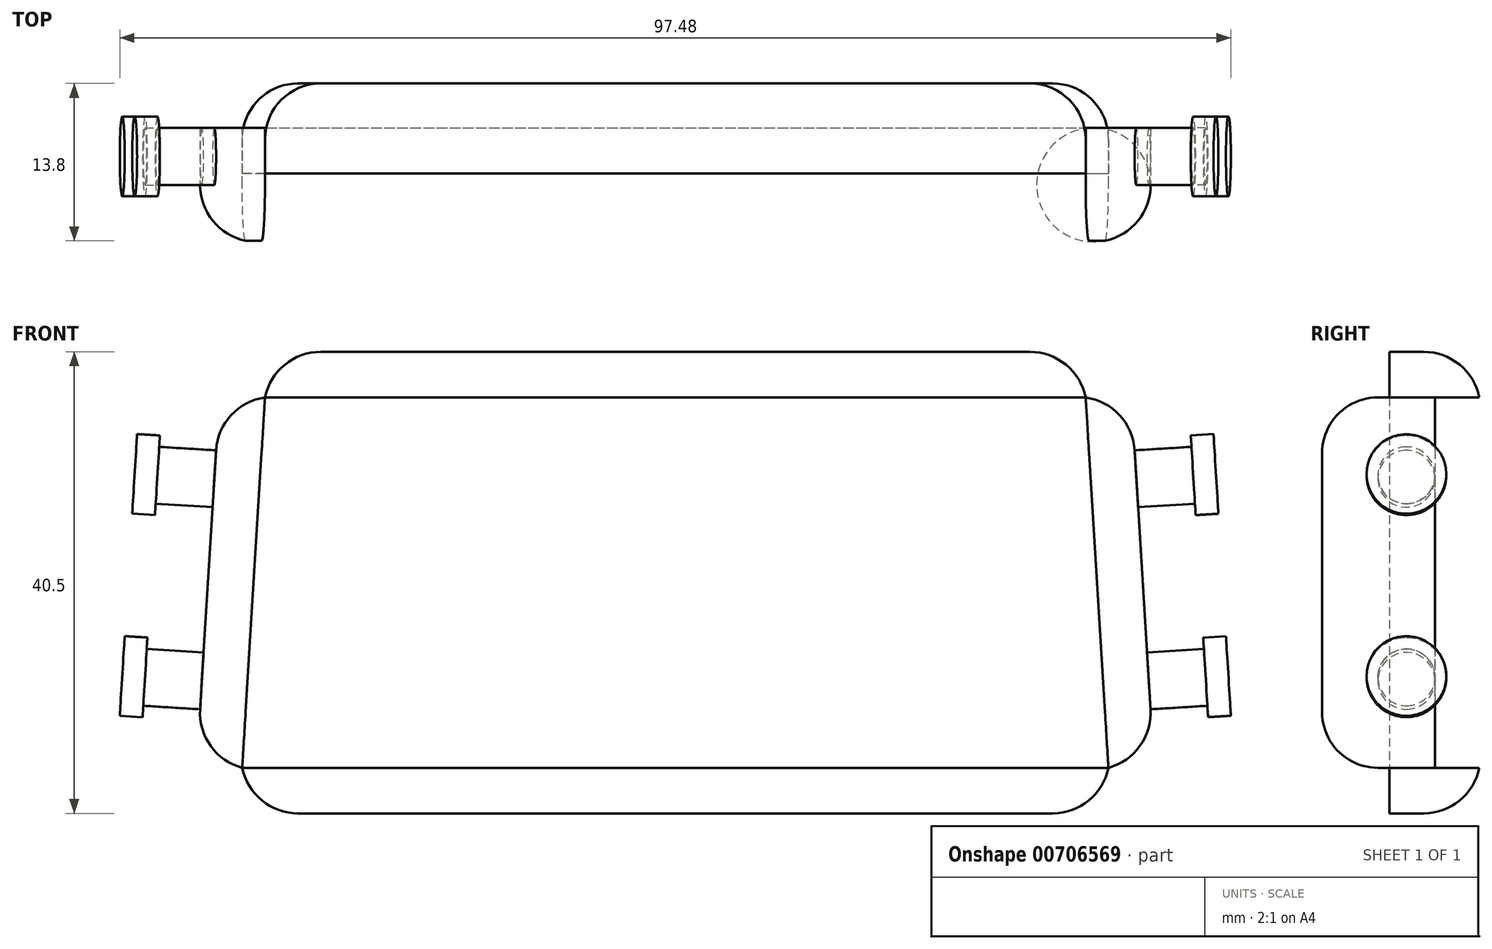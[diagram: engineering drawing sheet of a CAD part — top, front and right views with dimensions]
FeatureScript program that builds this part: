
annotation { "Feature Type Name" : "Feature", "Feature Type Description" : "" }
export const myFeature = defineFeature(function(context is Context, id is Id, definition is map)
    precondition{}
    {
        {
            var Q0;
            Q0=qCreatedBy(makeId("Front.planeOp"),FACE);
            var sketch = newSketch(context, id + "F0", { "sketchPlane" : qUnion([Q0])});
            skLineSegment(sketch, "E0", {"start": v(-36, 32.5) * mm, "end": v(36, 32.5) * mm});
            skLineSegment(sketch, "E1", {"start": v(-38, 0) * mm, "end": v(38, 0) * mm});
            skLineSegment(sketch, "E2", {"start": v(-36, 32.5) * mm, "end": v(-38, 0) * mm});
            skLineSegment(sketch, "E3", {"start": v(36, 32.5) * mm, "end": v(38, 0) * mm});
            skLineSegment(sketch, "E4", {"start": v(-36, 32.5) * mm, "end": v(-40, 32.75) * mm});
            skLineSegment(sketch, "E5", {"start": v(-38, 0) * mm, "end": v(-42, 0.25) * mm});
            skLineSegment(sketch, "E6", {"start": v(-42, 0.25) * mm, "end": v(-40, 32.75) * mm});
            skLineSegment(sketch, "E7", {"start": v(36, 32.5) * mm, "end": v(40, 32.75) * mm});
            skLineSegment(sketch, "E8", {"start": v(40, 32.75) * mm, "end": v(42, 0.25) * mm});
            skLineSegment(sketch, "E9", {"start": v(42, 0.25) * mm, "end": v(38, 0) * mm});
            skLineSegment(sketch, "E10", {"start": v(-38, 0) * mm, "end": v(-38, -4) * mm});
            skLineSegment(sketch, "E11", {"start": v(-38, -4) * mm, "end": v(38, -4) * mm});
            skLineSegment(sketch, "E12", {"start": v(38, -4) * mm, "end": v(38, 0) * mm});
            skLineSegment(sketch, "E13", {"start": v(-36, 32.5) * mm, "end": v(-36, 36.5) * mm});
            skLineSegment(sketch, "E14", {"start": v(-36, 36.5) * mm, "end": v(36, 36.5) * mm});
            skLineSegment(sketch, "E15", {"start": v(36, 36.5) * mm, "end": v(36, 32.5) * mm});
            skSolve(sketch);
        }
        {
            var Q0;
            Q0=makeQuery(id+"F0.imprint","IMPRINT",FACE,{"disambiguationData":[TD([[makeQuery(id+"F0.imprint","IMPRINT",EDGE,{"derivedFrom":sQuery(id+"F0.wireOp",EDGE,"E1")}),-1.0]])]});
            extrude(context, id + "F1", {"entities" : qUnion([Q0]), "oppositeDirection" : true, "depth" : 4 * mm, "offsetDistance" : 25 * mm, "hasSecondDirection" : true, "secondDirectionOppositeDirection" : false, "secondDirectionDepth" : 4 * mm});
        }
        {
            var Q0;
            Q0=makeQuery(id+"F0.imprint","IMPRINT",FACE,{"disambiguationData":[TD([[makeQuery(id+"F0.imprint","IMPRINT",EDGE,{"derivedFrom":sQuery(id+"F0.wireOp",EDGE,"E0")}),1.0]])]});
            extrude(context, id + "F2", {"entities" : qUnion([Q0]), "oppositeDirection" : true, "depth" : 4 * mm, "offsetDistance" : 25 * mm, "hasSecondDirection" : true, "secondDirectionOppositeDirection" : false, "secondDirectionDepth" : 4 * mm});
        }
        {
            var Q0;
            Q0=makeQuery(id+"F0.imprint","IMPRINT",FACE,{"disambiguationData":[TD([[makeQuery(id+"F0.imprint","IMPRINT",EDGE,{"derivedFrom":sQuery(id+"F0.wireOp",EDGE,"E2")}),-1.0]])]});
            extrude(context, id + "F3", {"entities" : qUnion([Q0]), "operationType" : NewBodyOperationType.ADD, "depth" : 10 * mm, "offsetDistance" : 25 * mm});
        }
        {
            var Q0;
            Q0=makeQuery(id+"F0.imprint","IMPRINT",FACE,{"disambiguationData":[TD([[makeQuery(id+"F0.imprint","IMPRINT",EDGE,{"derivedFrom":sQuery(id+"F0.wireOp",EDGE,"E3")}),1.0]])]});
            extrude(context, id + "F4", {"entities" : qUnion([Q0]), "depth" : 10 * mm, "offsetDistance" : 25 * mm});
        }
        {
            var Q0;
            Q0=makeQuery(id+"F0.imprint","IMPRINT",FACE,{"disambiguationData":[TD([[makeQuery(id+"F0.imprint","IMPRINT",EDGE,{"derivedFrom":sQuery(id+"F0.wireOp",EDGE,"E0")}),-1.0]])]});
            extrude(context, id + "F5", {"entities" : qUnion([Q0]), "depth" : 4 * mm, "offsetDistance" : 25 * mm});
        }
        {
            var Q0;
            Q0=makeQuery(id+"F4.opExtrude","SWEPT_EDGE",EDGE,{"disambiguationData":[OSD([sQuery(id+"F0.wireOp",EDGE,"E8"),sQuery(id+"F0.wireOp",EDGE,"E9")])]});
            fillet(context, id + "F6", {"entities" : qUnion([Q0]), "radius" : 5 * mm, "tangentPropagation" : true, "allowEdgeOverflow" : false});
        }
        {
            var Q0;
            Q0=makeQuery(id+"F1.opExtrude","SWEPT_EDGE",EDGE,{"disambiguationData":[OSD([sQuery(id+"F0.wireOp",EDGE,"E11"),sQuery(id+"F0.wireOp",EDGE,"E12")])]});
            fillet(context, id + "F7", {"entities" : qUnion([Q0]), "radius" : 5 * mm, "tangentPropagation" : true, "allowEdgeOverflow" : false});
        }
        {
            var Q0;
            Q0=makeQuery(id+"F1.opExtrude","SWEPT_EDGE",EDGE,{"disambiguationData":[OSD([sQuery(id+"F0.wireOp",EDGE,"E10"),sQuery(id+"F0.wireOp",EDGE,"E11")])]});
            fillet(context, id + "F8", {"entities" : qUnion([Q0]), "radius" : 5 * mm, "tangentPropagation" : true, "allowEdgeOverflow" : false});
        }
        {
            var Q0;
            Q0=makeQuery(id+"F3.opExtrude","SWEPT_EDGE",EDGE,{"disambiguationData":[OSD([sQuery(id+"F0.wireOp",EDGE,"E5"),sQuery(id+"F0.wireOp",EDGE,"E6")])]});
            fillet(context, id + "F9", {"entities" : qUnion([Q0]), "radius" : 5 * mm, "tangentPropagation" : true, "allowEdgeOverflow" : false});
        }
        {
            var Q0;
            Q0=makeQuery(id+"F3.opExtrude","SWEPT_EDGE",EDGE,{"disambiguationData":[OSD([sQuery(id+"F0.wireOp",EDGE,"E4"),sQuery(id+"F0.wireOp",EDGE,"E6")])]});
            fillet(context, id + "F10", {"entities" : qUnion([Q0]), "radius" : 5 * mm, "tangentPropagation" : true, "allowEdgeOverflow" : false});
        }
        {
            var Q0;
            Q0=makeQuery(id+"F2.opExtrude","SWEPT_EDGE",EDGE,{"disambiguationData":[OSD([sQuery(id+"F0.wireOp",EDGE,"E13"),sQuery(id+"F0.wireOp",EDGE,"E14")])]});
            fillet(context, id + "F11", {"entities" : qUnion([Q0]), "radius" : 5 * mm, "tangentPropagation" : true, "allowEdgeOverflow" : false});
        }
        {
            var Q0;
            Q0=makeQuery(id+"F2.opExtrude","SWEPT_EDGE",EDGE,{"disambiguationData":[OSD([sQuery(id+"F0.wireOp",EDGE,"E14"),sQuery(id+"F0.wireOp",EDGE,"E15")])]});
            fillet(context, id + "F12", {"entities" : qUnion([Q0]), "radius" : 5 * mm, "tangentPropagation" : true, "allowEdgeOverflow" : false});
        }
        {
            var Q0;
            Q0=makeQuery(id+"F4.opExtrude","SWEPT_EDGE",EDGE,{"disambiguationData":[OSD([sQuery(id+"F0.wireOp",EDGE,"E7"),sQuery(id+"F0.wireOp",EDGE,"E8")])]});
            fillet(context, id + "F13", {"entities" : qUnion([Q0]), "radius" : 5 * mm, "tangentPropagation" : true, "allowEdgeOverflow" : false});
        }
        {
            var Q0;
            Q0=makeQuery(id+"F4.opExtrude","CAP_EDGE",EDGE,{"disambiguationData":[OSD([sQuery(id+"F0.wireOp",EDGE,"E8")])],"isStart":false});
            fillet(context, id + "F14", {"entities" : qUnion([Q0]), "radius" : 5 * mm, "tangentPropagation" : true, "allowEdgeOverflow" : false});
        }
        {
            var Q0;
            Q0=makeQuery(id+"F3.opExtrude","CAP_EDGE",EDGE,{"disambiguationData":[OSD([sQuery(id+"F0.wireOp",EDGE,"E6")])],"isStart":false});
            fillet(context, id + "F15", {"entities" : qUnion([Q0]), "radius" : 5 * mm, "tangentPropagation" : true, "allowEdgeOverflow" : false});
        }
        {
            var Q0;
            Q0=makeQuery(id+"F2.opExtrude","CAP_EDGE",EDGE,{"disambiguationData":[OSD([sQuery(id+"F0.wireOp",EDGE,"E14")])],"isStart":false});
            fillet(context, id + "F16", {"entities" : qUnion([Q0]), "radius" : 5 * mm, "tangentPropagation" : true, "allowEdgeOverflow" : false});
        }
        {
            var Q0;
            Q0=makeQuery(id+"F1.opExtrude","CAP_EDGE",EDGE,{"disambiguationData":[OSD([sQuery(id+"F0.wireOp",EDGE,"E11")])],"isStart":false});
            fillet(context, id + "F17", {"entities" : qUnion([Q0]), "radius" : 5 * mm, "tangentPropagation" : true, "allowEdgeOverflow" : false});
        }
        {
            var Q0;
            Q0=makeQuery(id+"F3.opExtrude","SWEPT_FACE",FACE,{"disambiguationData":[OSD([sQuery(id+"F0.wireOp",EDGE,"E6")])]});
            var sketch = newSketch(context, id + "F18", { "sketchPlane" : qUnion([Q0])});
            skCircle(sketch, "E16", {"center": v(2.5, 5.06) * mm, "radius": 2.5 * mm});
            skPoint(sketch, "E16.first.point", {"position": v(5, 5.06) * mm});
            skPoint(sketch, "E16.second.point", {"position": v(2.5, 2.56) * mm});
            skPoint(sketch, "E16.third.point", {"position": v(0, 5.06) * mm});
            skCircle(sketch, "E17", {"center": v(2.5, 22.83) * mm, "radius": 2.5 * mm});
            skPoint(sketch, "E17.first.point", {"position": v(2.5, 25.33) * mm});
            skPoint(sketch, "E17.second.point", {"position": v(5, 22.83) * mm});
            skPoint(sketch, "E17.third.point", {"position": v(0, 22.83) * mm});
            skSolve(sketch);
        }
        {
            var Q0;
            {var subQ0=sQuery(id+"F18.wireOp",EDGE,"E17");var subQ1=sQuery(id+"F0.wireOp",EDGE,"E6");var subQ5=makeQuery(id+"F18.imprint","INTERSECT",VERTEX,{"derivedFrom":[makeQuery(id+"F3.opExtrude","CAP_EDGE",EDGE,{"disambiguationData":[OSD([subQ1])],"isStart":true}),subQ0]});Q0=makeQuery(id+"F18.imprint","IMPRINT",FACE,{"disambiguationData":[TD([[makeQuery(id+"F18.imprint","IMPRINT",EDGE,{"disambiguationData":[TD([[subQ5,-1.0]])],"derivedFrom":subQ0}),1.0]])]});}
            var Q1;
            {var subQ0=sQuery(id+"F18.wireOp",EDGE,"E16");var subQ1=sQuery(id+"F0.wireOp",EDGE,"E6");var subQ2=makeQuery(id+"F18.imprint","INTERSECT",VERTEX,{"derivedFrom":[makeQuery(id+"F3.opExtrude","CAP_EDGE",EDGE,{"disambiguationData":[OSD([subQ1])],"isStart":true}),subQ0]});Q1=makeQuery(id+"F18.imprint","IMPRINT",FACE,{"disambiguationData":[TD([[makeQuery(id+"F18.imprint","IMPRINT",EDGE,{"disambiguationData":[TD([[subQ2,1.0]])],"derivedFrom":subQ0}),1.0]])]});}
            var Q2;
            Q2=sQuery(id+"F18.wireOp",EDGE,"E16");
            var Q3;
            Q3=sQuery(id+"F18.wireOp",EDGE,"E17");
            extrude(context, id + "F19", {"entities" : qUnion([Q0, Q1]), "operationType" : NewBodyOperationType.ADD, "surfaceEntities" : qUnion([Q2, Q3]), "depth" : 5 * mm, "offsetDistance" : 25 * mm});
        }
        {
            var Q0;
            Q0=makeQuery(id+"F19.opExtrude","CAP_FACE",FACE,{"disambiguationData":[OSD([sQuery(id+"F18.wireOp",EDGE,"E16")])],"isStart":false});
            var sketch = newSketch(context, id + "F20", { "sketchPlane" : qUnion([Q0])});
            skCircle(sketch, "E18", {"center": v(2.5, 5.06) * mm, "radius": 3.5 * mm});
            skSolve(sketch);
        }
        {
            var Q0;
            Q0=makeQuery(id+"F20.imprint","IMPRINT",FACE,{"disambiguationData":[TD([[makeQuery(id+"F20.imprint","IMPRINT",EDGE,{"derivedFrom":sQuery(id+"F20.wireOp",EDGE,"E18")}),1.0]])]});
            var Q1;
            Q1=makeQuery(id+"F20.imprint","IMPRINT",FACE,{"disambiguationData":[TD([[makeQuery(id+"F20.imprint","IMPRINT",EDGE,{"derivedFrom":makeQuery(id+"F19.opExtrude","CAP_EDGE",EDGE,{"disambiguationData":[OSD([sQuery(id+"F18.wireOp",EDGE,"E16")])],"isStart":false})}),1.0]])]});
            var Q2;
            Q2=sQuery(id+"F20.wireOp",EDGE,"E18");
            extrude(context, id + "F21", {"entities" : qUnion([Q0, Q1]), "operationType" : NewBodyOperationType.ADD, "surfaceEntities" : qUnion([Q2]), "depth" : 2 * mm, "offsetDistance" : 25 * mm});
        }
        {
            var Q0;
            Q0=makeQuery(id+"F19.opExtrude","CAP_FACE",FACE,{"disambiguationData":[OSD([sQuery(id+"F18.wireOp",EDGE,"E17")])],"isStart":false});
            var sketch = newSketch(context, id + "F22", { "sketchPlane" : qUnion([Q0])});
            skCircle(sketch, "E19", {"center": v(2.5, 22.83) * mm, "radius": 3.5 * mm});
            skSolve(sketch);
        }
        {
            var Q0;
            Q0=makeQuery(id+"F22.imprint","IMPRINT",FACE,{"disambiguationData":[TD([[makeQuery(id+"F22.imprint","IMPRINT",EDGE,{"derivedFrom":sQuery(id+"F22.wireOp",EDGE,"E19")}),1.0]])]});
            var Q1;
            Q1=makeQuery(id+"F22.imprint","IMPRINT",FACE,{"disambiguationData":[TD([[makeQuery(id+"F22.imprint","IMPRINT",EDGE,{"derivedFrom":makeQuery(id+"F19.opExtrude","CAP_EDGE",EDGE,{"disambiguationData":[OSD([sQuery(id+"F18.wireOp",EDGE,"E17")])],"isStart":false})}),1.0]])]});
            var Q2;
            Q2=sQuery(id+"F22.wireOp",EDGE,"E19");
            extrude(context, id + "F23", {"entities" : qUnion([Q0, Q1]), "operationType" : NewBodyOperationType.ADD, "surfaceEntities" : qUnion([Q2]), "depth" : 2 * mm, "offsetDistance" : 25 * mm});
        }
        {
            var Q0;
            Q0=makeQuery(id+"F4.opExtrude","SWEPT_FACE",FACE,{"disambiguationData":[OSD([sQuery(id+"F0.wireOp",EDGE,"E8")])]});
            var sketch = newSketch(context, id + "F24", { "sketchPlane" : qUnion([Q0])});
            skCircle(sketch, "E20", {"center": v(-2.5, 5.06) * mm, "radius": 2.5 * mm});
            skPoint(sketch, "E20.first.point", {"position": v(-2.5, 2.56) * mm});
            skPoint(sketch, "E20.second.point", {"position": v(-5, 5.06) * mm});
            skPoint(sketch, "E20.third.point", {"position": v(0, 5.06) * mm});
            skCircle(sketch, "E21", {"center": v(-2.5, 22.83) * mm, "radius": 2.5 * mm});
            skPoint(sketch, "E21.first.point", {"position": v(-2.5, 25.33) * mm});
            skPoint(sketch, "E21.second.point", {"position": v(0, 22.83) * mm});
            skPoint(sketch, "E21.third.point", {"position": v(-5, 22.83) * mm});
            skSolve(sketch);
        }
        {
            var Q0;
            {var subQ0=sQuery(id+"F24.wireOp",EDGE,"E20");var subQ1=sQuery(id+"F0.wireOp",EDGE,"E8");var subQ4=makeQuery(id+"F24.imprint","INTERSECT",VERTEX,{"derivedFrom":[makeQuery(id+"F4.opExtrude","CAP_EDGE",EDGE,{"disambiguationData":[OSD([subQ1])],"isStart":true}),subQ0]});Q0=makeQuery(id+"F24.imprint","IMPRINT",FACE,{"disambiguationData":[TD([[makeQuery(id+"F24.imprint","IMPRINT",EDGE,{"disambiguationData":[TD([[subQ4,-1.0]])],"derivedFrom":subQ0}),1.0]])]});}
            var Q1;
            Q1=sQuery(id+"F24.wireOp",EDGE,"E20");
            extrude(context, id + "F25", {"entities" : qUnion([Q0]), "operationType" : NewBodyOperationType.ADD, "surfaceEntities" : qUnion([Q1]), "depth" : 5 * mm, "offsetDistance" : 25 * mm});
        }
        {
            var Q0;
            {var subQ0=sQuery(id+"F24.wireOp",EDGE,"E21");var subQ1=sQuery(id+"F0.wireOp",EDGE,"E8");var subQ4=makeQuery(id+"F24.imprint","INTERSECT",VERTEX,{"derivedFrom":[makeQuery(id+"F4.opExtrude","CAP_EDGE",EDGE,{"disambiguationData":[OSD([subQ1])],"isStart":true}),subQ0]});Q0=makeQuery(id+"F24.imprint","IMPRINT",FACE,{"disambiguationData":[TD([[makeQuery(id+"F24.imprint","IMPRINT",EDGE,{"disambiguationData":[TD([[subQ4,1.0]])],"derivedFrom":subQ0}),1.0]])]});}
            extrude(context, id + "F26", {"entities" : qUnion([Q0]), "operationType" : NewBodyOperationType.ADD, "depth" : 5 * mm, "offsetDistance" : 25 * mm});
        }
        {
            var Q0;
            Q0=makeQuery(id+"F25.opExtrude","CAP_FACE",FACE,{"disambiguationData":[OSD([sQuery(id+"F24.wireOp",EDGE,"E20")])],"isStart":false});
            var sketch = newSketch(context, id + "F27", { "sketchPlane" : qUnion([Q0])});
            skCircle(sketch, "E22", {"center": v(-2.5, 5.06) * mm, "radius": 3.5 * mm});
            skSolve(sketch);
        }
        {
            var Q0;
            Q0 = qSketchRegion(id + "F27", true);
            extrude(context, id + "F28", {"entities" : qUnion([Q0]), "operationType" : NewBodyOperationType.ADD, "depth" : 2 * mm, "offsetDistance" : 25 * mm});
        }
        {
            var Q0;
            Q0=makeQuery(id+"F26.opExtrude","CAP_FACE",FACE,{"disambiguationData":[OSD([sQuery(id+"F24.wireOp",EDGE,"E21")])],"isStart":false});
            var sketch = newSketch(context, id + "F29", { "sketchPlane" : qUnion([Q0])});
            skCircle(sketch, "E23", {"center": v(-2.5, 22.83) * mm, "radius": 3.5 * mm});
            skSolve(sketch);
        }
        {
            var Q0;
            Q0 = qSketchRegion(id + "F29", true);
            extrude(context, id + "F30", {"entities" : qUnion([Q0]), "operationType" : NewBodyOperationType.ADD, "depth" : 2 * mm, "offsetDistance" : 25 * mm});
        }
    });
